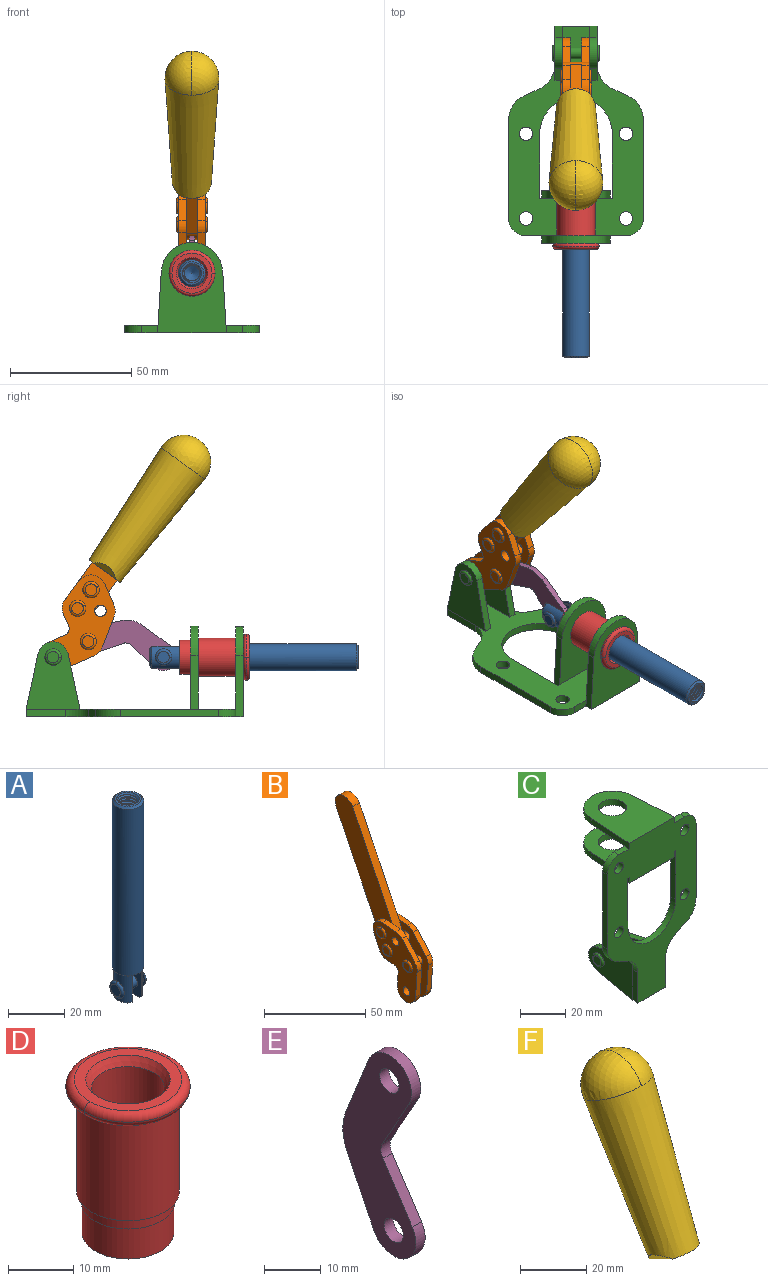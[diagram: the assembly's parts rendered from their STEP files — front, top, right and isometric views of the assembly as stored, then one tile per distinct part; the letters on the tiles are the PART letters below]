
ASSEMBLY  parts=6 mates=6
PART A: 48 faces, bbox 12.6x11.1x86.1 mm
  f0: torus R=2.41mm, axis (-1,0,0), area 15mm2, adj f30,f32,f34
  f1: torus R=2.41mm, axis (-1,0,0), area 15mm2, adj f29,f31,f33
  f2: cylinder r=5.54mm len=72.39mm, axis (0,0,1), area 2518.5mm2, adj f3,f4,f42,f43
  f3: cone r=5.54mm half-angle=45deg, axis (0,0,1), area 7.6mm2, adj f2,f5,f41
  f4: cone r=5.54mm half-angle=45deg, axis (0,0,-1), area 34.9mm2, adj f2,f39
  f5: cylinder r=5.08mm len=11.48mm, axis (0,0,1), area 108.3mm2, adj f3,f7,f8,f41
  f6: cylinder r=2.41mm len=4.83mm, axis (-1,0,0), area 71.2mm2, adj f40,f41
  f7: cylinder r=2.41mm len=4.83mm, axis (-1,0,0), area 7.6mm2, adj f5,f34
  f8: cone r=5.08mm half-angle=45deg, axis (0,0,1), area 10.6mm2, adj f5,f37,f41
  f9: cone r=3.98mm half-angle=45deg, axis (0,0,1), area 17.6mm2, adj f27,f39,f45,f46,f47
  f10: cylinder r=2.41mm len=4.83mm, axis (-1,0,0), area 7.6mm2, adj f33,f38
  f11: cylinder r=3.2mm len=6.4mm, axis (0,0,1), area 78.4mm2, adj f12,f28,f44,f45,f47
  f12: cylinder r=3.2mm len=6.4mm, axis (0,0,1), area 10.5mm2, adj f11,f13,f45,f47
  f13: cylinder r=3.2mm len=6.4mm, axis (0,0,1), area 10.5mm2, adj f12,f14,f45,f47
  f14: cylinder r=3.2mm len=6.4mm, axis (0,0,1), area 10.5mm2, adj f13,f15,f45,f47
  f15: cylinder r=3.2mm len=6.4mm, axis (0,0,1), area 10.5mm2, adj f14,f16,f45,f47
  f16: cylinder r=3.2mm len=6.4mm, axis (0,0,1), area 10.5mm2, adj f15,f17,f45,f47
  f17: cylinder r=3.2mm len=6.4mm, axis (0,0,1), area 10.5mm2, adj f16,f18,f45,f47
  f18: cylinder r=3.2mm len=6.4mm, axis (0,0,1), area 10.5mm2, adj f17,f19,f45,f47
  f19: cylinder r=3.2mm len=6.4mm, axis (0,0,1), area 10.5mm2, adj f18,f20,f45,f47
  f20: cylinder r=3.2mm len=6.4mm, axis (0,0,1), area 10.5mm2, adj f19,f21,f45,f47
  f21: cylinder r=3.2mm len=6.4mm, axis (0,0,1), area 10.5mm2, adj f20,f22,f45,f47
  f22: cylinder r=3.2mm len=6.4mm, axis (0,0,1), area 10.5mm2, adj f21,f23,f45,f47
  f23: cylinder r=3.2mm len=6.4mm, axis (0,0,1), area 10.5mm2, adj f22,f24,f45,f47
  f24: cylinder r=3.2mm len=6.4mm, axis (0,0,1), area 10.5mm2, adj f23,f25,f45,f47
  f25: cylinder r=3.2mm len=6.4mm, axis (0,0,1), area 10.5mm2, adj f24,f26,f45,f47
  f26: cylinder r=3.2mm len=6.4mm, axis (0,0,1), area 10.5mm2, adj f25,f27,f45,f47
  f27: cylinder r=3.2mm len=6.4mm, axis (0,0,1), area 7.4mm2, adj f9,f26,f45,f47
  f28: cone r=3.2mm half-angle=60deg, axis (0,0,1), area 37.2mm2, adj f11
  f29: plane 4.83x4.83mm, normal (-1,0,0), area 18.3mm2, adj f1,f31
  f30: plane 4.83x4.83mm, normal (1,0,0), area 18.3mm2, adj f0,f32
  f31: torus R=2.41mm, axis (-1,0,0), area 15mm2, adj f1,f29,f33
  f32: torus R=2.41mm, axis (-1,0,0), area 15mm2, adj f0,f30,f34
  f33: plane 6.83x6.83mm, normal (1,0,0), area 18.3mm2, adj f1,f10,f31
  f34: plane 6.83x6.83mm, normal (-1,0,0), area 18.3mm2, adj f0,f7,f32
  f35: cone r=5.08mm half-angle=45deg, axis (0,0,1), area 10.6mm2, adj f36,f38,f40
  f36: plane 7.25x1.97mm, normal (0,0,-1), area 10mm2, adj f35,f40
  f37: plane 7.25x1.97mm, normal (0,0,-1), area 10mm2, adj f8,f41
  f38: cylinder r=5.08mm len=11.48mm, axis (0,0,1), area 108.3mm2, adj f10,f35,f40,f42
  f39: plane 9.55x9.55mm, normal (0,0,1), area 22mm2, adj f4,f9
  f40: plane 12.76x10.09mm, normal (1,0,0), area 95.7mm2, adj f6,f35,f36,f38,f42,f43
  f41: plane 12.76x10.09mm, normal (-1,0,0), area 95.7mm2, adj f3,f5,f6,f8,f37,f43
  f42: cone r=5.54mm half-angle=45deg, axis (0,0,1), area 7.6mm2, adj f2,f38,f40
  f43: plane 11.07x4.7mm, normal (0,0,-1), area 50.4mm2, adj f2,f40,f41
  f44: plane 0.89x0.62mm, normal (-1,0,0), area 0.3mm2, adj f11,f45,f46,f47
  f45: bspline ~24.8x7.63mm, area 266.6mm2, adj f9,f11,f12,f13,f14,f15,f16,f17
  f46: bspline ~24.87x7.63mm, area 73.6mm2, adj f9,f44,f45,f47
  f47: bspline ~24.98x7.63mm, area 272.5mm2, adj f9,f11,f12,f13,f14,f15,f16,f17
PART B: 59 faces, bbox 12.9x60.2x99.6 mm
  f0: torus R=2.39mm, axis (-1,0,0), area 14.9mm2, adj f20,f43,f51
  f1: torus R=2.39mm, axis (-1,0,0), area 14.9mm2, adj f19,f42,f51
  f2: torus R=2.39mm, axis (-1,0,0), area 14.9mm2, adj f18,f35,f51
  f3: torus R=2.39mm, axis (-1,0,0), area 14.9mm2, adj f14,f17,f23
  f4: torus R=2.39mm, axis (-1,0,0), area 14.9mm2, adj f13,f16,f23
  f5: torus R=2.39mm, axis (-1,0,0), area 14.9mm2, adj f12,f15,f23
  f6: cylinder r=2.39mm len=4.78mm, axis (1,0,0), area 46.5mm2, adj f48,f50,f51
  f7: cylinder r=2.39mm len=4.78mm, axis (1,0,0), area 46.5mm2, adj f50,f51
  f8: cylinder r=6.35mm len=12.68mm, axis (1,0,0), area 61.8mm2, adj f38,f39,f50,f51
  f9: cylinder r=2.39mm len=4.78mm, axis (-1,0,0), area 70.5mm2, adj f46,f50
  f10: cylinder r=2.39mm len=4.78mm, axis (-1,0,0), area 46.5mm2, adj f23,f45,f46
  f11: cylinder r=2.39mm len=4.78mm, axis (-1,0,0), area 46.5mm2, adj f23,f46
  f12: plane 4.78x4.78mm, normal (1,0,0), area 17.9mm2, adj f5,f15
  f13: plane 4.78x4.78mm, normal (1,0,0), area 17.9mm2, adj f4,f16
  f14: plane 4.78x4.78mm, normal (1,0,0), area 17.9mm2, adj f3,f17
  f15: torus R=2.39mm, axis (-1,0,0), area 14.9mm2, adj f5,f12,f23
  f16: torus R=2.39mm, axis (-1,0,0), area 14.9mm2, adj f4,f13,f23
  f17: torus R=2.39mm, axis (-1,0,0), area 14.9mm2, adj f3,f14,f23
  f18: plane 4.78x4.78mm, normal (-1,0,0), area 17.9mm2, adj f2,f35
  f19: plane 4.78x4.78mm, normal (-1,0,0), area 17.9mm2, adj f1,f42
  f20: plane 4.78x4.78mm, normal (-1,0,0), area 17.9mm2, adj f0,f43
  f21: plane 2.26x0.2mm, normal (1,0,0), area 0.2mm2, adj f31,f44
  f22: plane 2.26x0.2mm, normal (-1,0,0), area 0.2mm2, adj f41,f44
  f23: plane 39.37x30.77mm, normal (1,0,0), area 565.5mm2, adj f3,f4,f5,f10,f11,f15,f16,f17
  f24: cylinder r=6.1mm len=4.15mm, axis (-1,0,0), area 14.7mm2, adj f23,f25,f32,f46
  f25: plane 10.25x9.01mm, normal (0,-0.75,0.66), area 42.3mm2, adj f23,f24,f26,f46
  f26: cylinder r=6.35mm len=4.64mm, axis (-1,0,0), area 15.6mm2, adj f23,f25,f27,f46
  f27: plane 15.84x3.1mm, normal (0,-1,-0.07), area 49.2mm2, adj f23,f26,f28,f46
  f28: cylinder r=6.35mm len=12.68mm, axis (-1,0,0), area 61.8mm2, adj f23,f27,f29,f46
  f29: plane 8.11x3.1mm, normal (0,1,0.07), area 25.2mm2, adj f23,f28,f30,f46
  f30: cylinder r=3.05mm len=3.25mm, axis (-1,0,0), area 14.8mm2, adj f23,f29,f31,f46
  f31: plane 5.99x3.1mm, normal (0,0.07,-1), area 18.6mm2, adj f21,f23,f30,f44,f46
  f32: plane 9.5x3.1mm, normal (0,-0.07,1), area 29.5mm2, adj f23,f24,f33,f46,f47
  f33: cylinder r=6.1mm len=8.63mm, axis (-1,0,0), area 39.1mm2, adj f23,f32,f34,f47
  f34: plane 8.65x3.96mm, normal (0,0.91,-0.42), area 29.5mm2, adj f23,f33,f44,f47
  f35: torus R=2.39mm, axis (-1,0,0), area 14.9mm2, adj f2,f18,f51
  f36: plane 10.25x9.01mm, normal (0,-0.75,0.66), area 42.3mm2, adj f37,f49,f50,f51
  f37: cylinder r=6.35mm len=4.64mm, axis (1,0,0), area 15.6mm2, adj f36,f38,f50,f51
  f38: plane 15.84x3.1mm, normal (0,-1,-0.07), area 49.2mm2, adj f8,f37,f50,f51
  f39: plane 8.11x3.1mm, normal (0,1,0.07), area 25.2mm2, adj f8,f40,f50,f51
  f40: cylinder r=3.05mm len=3.25mm, axis (1,0,0), area 14.8mm2, adj f39,f41,f50,f51
  f41: plane 5.99x3.1mm, normal (0,0.07,-1), area 18.6mm2, adj f22,f40,f44,f50,f51
  f42: torus R=2.39mm, axis (-1,0,0), area 14.9mm2, adj f1,f19,f51
  f43: torus R=2.39mm, axis (-1,0,0), area 14.9mm2, adj f0,f20,f51
  f44: cylinder r=6.35mm len=12.12mm, axis (-1,0,0), area 128.9mm2, adj f21,f22,f23,f31,f34,f41,f46,f47
  f45: plane 2.65x1.35mm, normal (1,0,0), area 1mm2, adj f10,f55
  f46: plane 39.08x20.42mm, normal (-1,0,0), area 412.5mm2, adj f9,f10,f11,f24,f25,f26,f27,f28
  f47: plane 77.62x39.82mm, normal (1,0,0), area 850mm2, adj f32,f33,f34,f44,f53,f54,f55
  f48: plane 2.65x1.35mm, normal (-1,0,0), area 1mm2, adj f6,f55
  f49: cylinder r=6.1mm len=4.15mm, axis (1,0,0), area 14.7mm2, adj f36,f50,f51,f56
  f50: plane 39.08x20.42mm, normal (1,0,0), area 412.5mm2, adj f6,f7,f8,f9,f36,f37,f38,f39
  f51: plane 39.37x30.77mm, normal (-1,0,0), area 565.5mm2, adj f0,f1,f2,f6,f7,f8,f35,f36
  f52: plane 8.65x3.96mm, normal (0,0.91,-0.42), area 29.5mm2, adj f44,f51,f57,f58
  f53: plane 68.49x33.4mm, normal (0,0.9,-0.44), area 358.1mm2, adj f44,f47,f54,f58
  f54: cylinder r=6.35mm len=12.06mm, axis (1,0,0), area 93.7mm2, adj f47,f53,f55,f58
  f55: plane 68.49x33.4mm, normal (0,-0.9,0.44), area 358.1mm2, adj f44,f45,f46,f47,f48,f50,f54,f58
  f56: plane 9.5x3.1mm, normal (0,-0.07,1), area 29.5mm2, adj f49,f50,f51,f57,f58
  f57: cylinder r=6.1mm len=8.63mm, axis (1,0,0), area 39.1mm2, adj f51,f52,f56,f58
  f58: plane 77.62x39.82mm, normal (-1,0,0), area 850mm2, adj f44,f52,f53,f54,f55,f56,f57
PART C: 55 faces, bbox 55.7x37.4x89.8 mm
  f0: torus R=2.41mm, axis (-1,0,0), area 15mm2, adj f11,f15,f25
  f1: torus R=2.41mm, axis (-1,0,0), area 15mm2, adj f10,f12,f22
  f2: cylinder r=2.78mm len=5.56mm, axis (0,-1,0), area 54.2mm2, adj f30,f54
  f3: cylinder r=14.99mm len=29.97mm, axis (0,-1,0), area 145.9mm2, adj f30,f49,f53,f54
  f4: cylinder r=2.78mm len=5.56mm, axis (0,-1,0), area 54.2mm2, adj f30,f54
  f5: cylinder r=2.78mm len=5.56mm, axis (0,-1,0), area 54.2mm2, adj f30,f54
  f6: cylinder r=2.78mm len=5.56mm, axis (0,-1,0), area 54.2mm2, adj f30,f54
  f7: cylinder r=6.35mm len=12.7mm, axis (0,0,1), area 123.6mm2, adj f27,f51
  f8: cylinder r=6.35mm len=12.7mm, axis (0,0,-1), area 124.7mm2, adj f21,f35
  f9: cylinder r=2.41mm len=11.18mm, axis (-1,0,0), area 169.4mm2, adj f16,f19
  f10: plane 4.83x4.83mm, normal (1,0,0), area 18.3mm2, adj f1,f12
  f11: plane 4.83x4.83mm, normal (-1,0,0), area 18.3mm2, adj f0,f15
  f12: torus R=2.41mm, axis (-1,0,0), area 15mm2, adj f1,f10,f22
  f13: cylinder r=6.35mm len=12.41mm, axis (1,0,0), area 53.4mm2, adj f18,f19,f22,f23
  f14: cylinder r=6.35mm len=12.41mm, axis (-1,0,0), area 53.4mm2, adj f16,f17,f24,f25
  f15: torus R=2.41mm, axis (-1,0,0), area 15mm2, adj f0,f11,f25
  f16: plane 27.86x22.35mm, normal (1,0,0), area 425.4mm2, adj f9,f14,f17,f24,f30
  f17: plane 22.86x4.97mm, normal (0,0.21,0.98), area 72.5mm2, adj f14,f16,f25,f30
  f18: plane 22.86x4.97mm, normal (0,0.21,0.98), area 72.5mm2, adj f13,f19,f22,f30
  f19: plane 27.86x22.35mm, normal (-1,0,0), area 425.4mm2, adj f9,f13,f18,f23,f30
  f20: cylinder r=12.7mm len=25.35mm, axis (0,0,-1), area 119.8mm2, adj f21,f34,f35,f36
  f21: plane 34.21x28.07mm, normal (0,0,-1), area 702.4mm2, adj f8,f20,f30,f34,f36
  f22: plane 27.96x22.45mm, normal (1,0,0), area 407.2mm2, adj f1,f12,f13,f18,f23,f30,f42,f43
  f23: plane 22.86x4.97mm, normal (0,0.21,-0.98), area 72.5mm2, adj f13,f19,f22,f44
  f24: plane 22.86x4.97mm, normal (0,0.21,-0.98), area 72.5mm2, adj f14,f16,f25,f44
  f25: plane 27.86x22.35mm, normal (-1,0,0), area 407.1mm2, adj f0,f14,f15,f17,f24,f30,f45,f46
  f26: plane 3.1x0.95mm, normal (0,0,-1), area 2.7mm2, adj f30,f49,f50,f54
  f27: plane 34.21x28.07mm, normal (0,0,1), area 702.4mm2, adj f7,f28,f30,f50,f52
  f28: cylinder r=12.7mm len=25.35mm, axis (0,0,1), area 118.8mm2, adj f27,f50,f51,f52
  f29: plane 3.1x0.95mm, normal (0,0,-1), area 2.7mm2, adj f30,f52,f53,f54
  f30: plane 86.54x55.63mm, normal (0,1,0), area 2362.9mm2, adj f2,f3,f4,f5,f6,f16,f17,f18
  f31: plane 40.56x3.1mm, normal (-1,0,0), area 125.7mm2, adj f30,f32,f48,f54
  f32: cylinder r=7.11mm len=7.11mm, axis (0,-1,0), area 34.6mm2, adj f30,f31,f33,f54
  f33: plane 6.67x3.1mm, normal (0,0,1), area 20.4mm2, adj f30,f32,f34,f54
  f34: plane 25.39x3.13mm, normal (-1,0.06,0), area 79.5mm2, adj f20,f21,f33,f35,f54
  f35: plane 37.31x28.45mm, normal (0,0,1), area 789.9mm2, adj f8,f20,f34,f36,f54
  f36: plane 25.39x3.13mm, normal (1,0.06,0), area 79.5mm2, adj f20,f21,f35,f37,f54
  f37: plane 6.67x3.1mm, normal (0,0,1), area 20.4mm2, adj f30,f36,f38,f54
  f38: cylinder r=7.11mm len=7.11mm, axis (0,-1,0), area 34.6mm2, adj f30,f37,f39,f54
  f39: plane 40.56x3.1mm, normal (1,0,0), area 125.7mm2, adj f30,f38,f40,f54
  f40: cylinder r=11.18mm len=10.16mm, axis (0,-1,0), area 39.5mm2, adj f30,f39,f41,f54
  f41: plane 6.09x3.1mm, normal (0.42,0,-0.91), area 20.8mm2, adj f30,f40,f42,f54
  f42: cylinder r=11.18mm len=9.41mm, axis (0,-1,0), area 37.2mm2, adj f22,f30,f41,f43,f54
  f43: plane 16.5x3.1mm, normal (1,0,0), area 51.1mm2, adj f22,f42,f44,f54
  f44: plane 17.37x3.1mm, normal (0,0,-1), area 53.8mm2, adj f23,f24,f30,f43,f45,f54
  f45: plane 16.5x3.1mm, normal (-1,0,0), area 51.1mm2, adj f25,f44,f46,f54
  f46: cylinder r=11.18mm len=9.41mm, axis (0,-1,0), area 37.2mm2, adj f25,f30,f45,f47,f54
  f47: plane 6.09x3.1mm, normal (-0.42,0,-0.91), area 20.8mm2, adj f30,f46,f48,f54
  f48: cylinder r=11.18mm len=10.16mm, axis (0,-1,0), area 39.5mm2, adj f30,f31,f47,f54
  f49: plane 26.54x3.1mm, normal (-1,0,0), area 82.3mm2, adj f3,f26,f30,f54
  f50: plane 25.39x3.1mm, normal (1,0.06,0), area 78.8mm2, adj f26,f27,f28,f51,f54
  f51: plane 37.31x28.45mm, normal (0,0,-1), area 789.9mm2, adj f7,f28,f50,f52,f54
  f52: plane 25.39x3.1mm, normal (-1,0.06,0), area 78.8mm2, adj f27,f28,f29,f51,f54
  f53: plane 26.54x3.1mm, normal (1,0,0), area 82.3mm2, adj f3,f29,f30,f54
  f54: plane 89.66x55.63mm, normal (0,-1,0), area 2678.5mm2, adj f2,f3,f4,f5,f6,f26,f29,f31
PART D: 15 faces, bbox 20.6x20.6x28.7 mm
  f0: torus R=8.26mm, axis (0,0,1), area 56.8mm2, adj f1,f10,f12
  f1: torus R=8.26mm, axis (0,0,1), area 56.8mm2, adj f0,f6,f13
  f2: cylinder r=5.59mm len=25.91mm, axis (0,0,1), area 909.6mm2, adj f3,f4
  f3: cone r=6.86mm half-angle=45deg, axis (0,0,-1), area 70.2mm2, adj f2,f14
  f4: cone r=6.47mm half-angle=30deg, axis (0,0,1), area 66.7mm2, adj f2,f13
  f5: cylinder r=7.04mm len=14.07mm, axis (0,0,1), area 252.6mm2, adj f11,f14
  f6: torus R=8.26mm, axis (0,0,1), area 56.8mm2, adj f1,f12,f13
  f7: cylinder r=7.16mm len=14.33mm, axis (0,0,1), area 91.5mm2, adj f9,f11
  f8: cylinder r=7.86mm len=18.42mm, axis (0,0,1), area 909.6mm2, adj f9,f10
  f9: plane 15.72x15.72mm, normal (0,0,-1), area 33mm2, adj f7,f8
  f10: plane 16.51x16.51mm, normal (0,0,-1), area 19.9mm2, adj f0,f8,f12
  f11: plane 14.33x14.33mm, normal (0,0,-1), area 5.7mm2, adj f5,f7
  f12: torus R=8.26mm, axis (0,0,1), area 56.8mm2, adj f0,f6,f10
  f13: plane 16.51x16.51mm, normal (0,0,1), area 82.7mm2, adj f1,f4,f6
  f14: plane 14.07x14.07mm, normal (0,0,-1), area 7.8mm2, adj f3,f5
PART E: 12 faces, bbox 2.3x18.2x42.8 mm
  f0: cylinder r=2.4mm len=4.8mm, axis (1,0,0), area 34.9mm2, adj f4,f11
  f1: cylinder r=10.41mm len=8.47mm, axis (1,0,0), area 20.2mm2, adj f4,f9,f10,f11
  f2: cylinder r=3.05mm len=3.16mm, axis (1,0,0), area 7.7mm2, adj f4,f6,f7,f11
  f3: cylinder r=2.4mm len=4.8mm, axis (1,0,0), area 34.9mm2, adj f4,f11
  f4: plane 42.81x18.23mm, normal (-1,0,0), area 414.1mm2, adj f0,f1,f2,f3,f5,f6,f7,f8
  f5: cylinder r=5.54mm len=10.67mm, axis (1,0,0), area 41.8mm2, adj f4,f6,f10,f11
  f6: plane 11.66x6.53mm, normal (0,-0.87,-0.49), area 30.9mm2, adj f2,f4,f5,f11
  f7: plane 11.17x7.33mm, normal (0,-0.84,0.55), area 30.9mm2, adj f2,f4,f8,f11
  f8: cylinder r=5.54mm len=10.51mm, axis (1,0,0), area 41.8mm2, adj f4,f7,f9,f11
  f9: plane 13.67x6.67mm, normal (0,0.9,-0.44), area 35.1mm2, adj f1,f4,f8,f11
  f10: plane 14.1x5.7mm, normal (0,0.93,0.37), area 35.1mm2, adj f1,f4,f5,f11
  f11: plane 42.81x18.23mm, normal (1,0,0), area 414.1mm2, adj f0,f1,f2,f3,f5,f6,f7,f8
PART F: 11 faces, bbox 22.3x42.6x64.5 mm
  f0: sphere r=11.13mm, area 411.4mm2, adj f1,f8
  f1: cone r=11.11mm half-angle=3.3deg, axis (0,0.44,0.9), area 3251.8mm2, adj f0,f7,f8,f9,f10
  f2: cylinder r=6.16mm len=11.7mm, axis (1,0,0), area 89.5mm2, adj f3,f4,f5,f6
  f3: plane 60.23x36.75mm, normal (-1,0,0), area 763.6mm2, adj f2,f4,f6,f10
  f4: plane 51.37x25.05mm, normal (0,0.9,-0.44), area 264.2mm2, adj f2,f3,f5,f10
  f5: plane 60.23x36.75mm, normal (1,0,0), area 763.6mm2, adj f2,f4,f6,f10
  f6: plane 51.37x25.05mm, normal (0,-0.9,0.44), area 264.2mm2, adj f2,f3,f5,f10
  f7: plane 9.95x5.95mm, normal (0.71,-0.31,-0.64), area 25.8mm2, adj f1,f10
  f8: sphere r=11.13mm, area 411.4mm2, adj f0,f1
  f9: plane 9.95x5.95mm, normal (-0.71,-0.31,-0.64), area 25.8mm2, adj f1,f10
  f10: plane 14.27x11.38mm, normal (0,-0.44,-0.9), area 106.7mm2, adj f1,f3,f4,f5,f6,f7,f9
PLACE A rot(axis=(1,0,0),90deg) t=(0,11.41,0)mm
PLACE B rot(axis=(1,0,0),62deg) t=(0,1.63,17.96)mm
PLACE C rot(axis=(1,0,0),90deg) t=(0,9.43,0)mm fixed
PLACE D rot(axis=(1,0,0),90deg) t=(0,9.43,0)mm
PLACE E rot(axis=(1,0,0),103.7deg) t=(0,16.82,4.38)mm
PLACE F rot(axis=(1,0,0),62deg) t=(-0.04,1.63,17.96)mm
MATE fastened D.f2 <-> C.f7  axis (0,-1,0) through (0,-36.96,24.61)mm
MATE fastened B.f54 <-> F.f2  axis (1,0,0) through (-2.35,-13.35,106.41)mm
MATE revolute E.f3 <-> B.f4  axis (1,0,0) through (0,27.02,31.07)mm
MATE revolute B.f7 <-> C.f0  axis (-1,0,0) through (0,41.52,24.61)mm
MATE slider A.f2 <-> D.f2  axis (0,-1,0) through (0,-47.37,24.61)mm
MATE revolute A.f6 <-> E.f5  axis (-1,0,0) through (0,-4.06,24.61)mm
